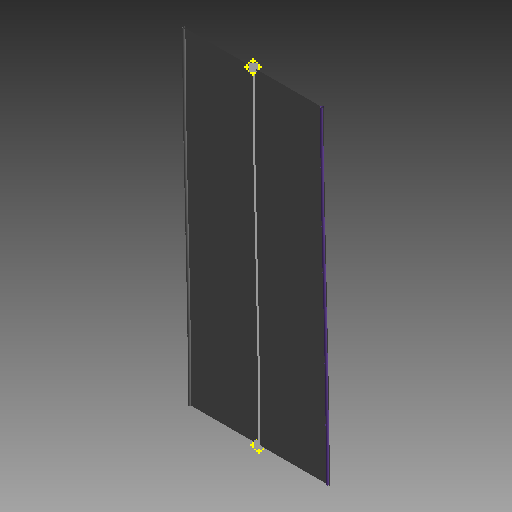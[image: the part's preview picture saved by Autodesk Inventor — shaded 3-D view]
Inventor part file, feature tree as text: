
AUTODESK INVENTOR PART (.ipt)
format: ipt  version: 2019 (Build 230136000, 136)  size: 125,952 bytes
history: native  units: mm (DEFAULTED — no unit token found)
features: other x6, sketch x3, sweep x3
ambient origin geometry x8: Origin, YZ Plane, XZ Plane, XY Plane, X Axis, Y Axis, Z Axis, Center Point
bodies: Body1 (feature_tree), Body2 (feature_tree), Body3 (feature_tree)
feature tree (12):
  other  "Work Point1"
  other  "Work Point2"
  other  "RibbonCable1"
  sketch  "Sketch1"  dims[d0=0.0mm d1=0.0mm d2=0.0mm d3=0.0mm]
  sketch  "Sketch2"  dims[d4=0.0mm d5=0.0mm]
  sketch  "Sketch3"
  other  "Srf1"
  other  "Srf2"
  other  "Srf3"
  sweep  "SweepSrf1"
  sweep  "SweepSrf2"
  sweep  "SweepSrf3"
